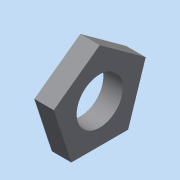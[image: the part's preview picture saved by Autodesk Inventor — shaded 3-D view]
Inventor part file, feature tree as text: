
AUTODESK INVENTOR PART (.ipt)
format: ipt  version: 2015 (Build 190159000, 159)  size: 76,288 bytes
history: native  units: in
note: dims shown in document units (in); Inventor stores cm internally (conversion verified against a paired STEP export)
features: extrude x1, sketch x1
ambient origin geometry x8: Origin, YZ Plane, XZ Plane, XY Plane, X Axis, Y Axis, Z Axis, Center Point
bodies: Solid1 (feature_tree)
feature tree (2):
  extrude  "Extrusion1"  Depth=0.083in TaperAngle=0.0deg
  sketch  "Sketch1"  dims[d0=0.1969in d1=0.083in d2=0.0in]
